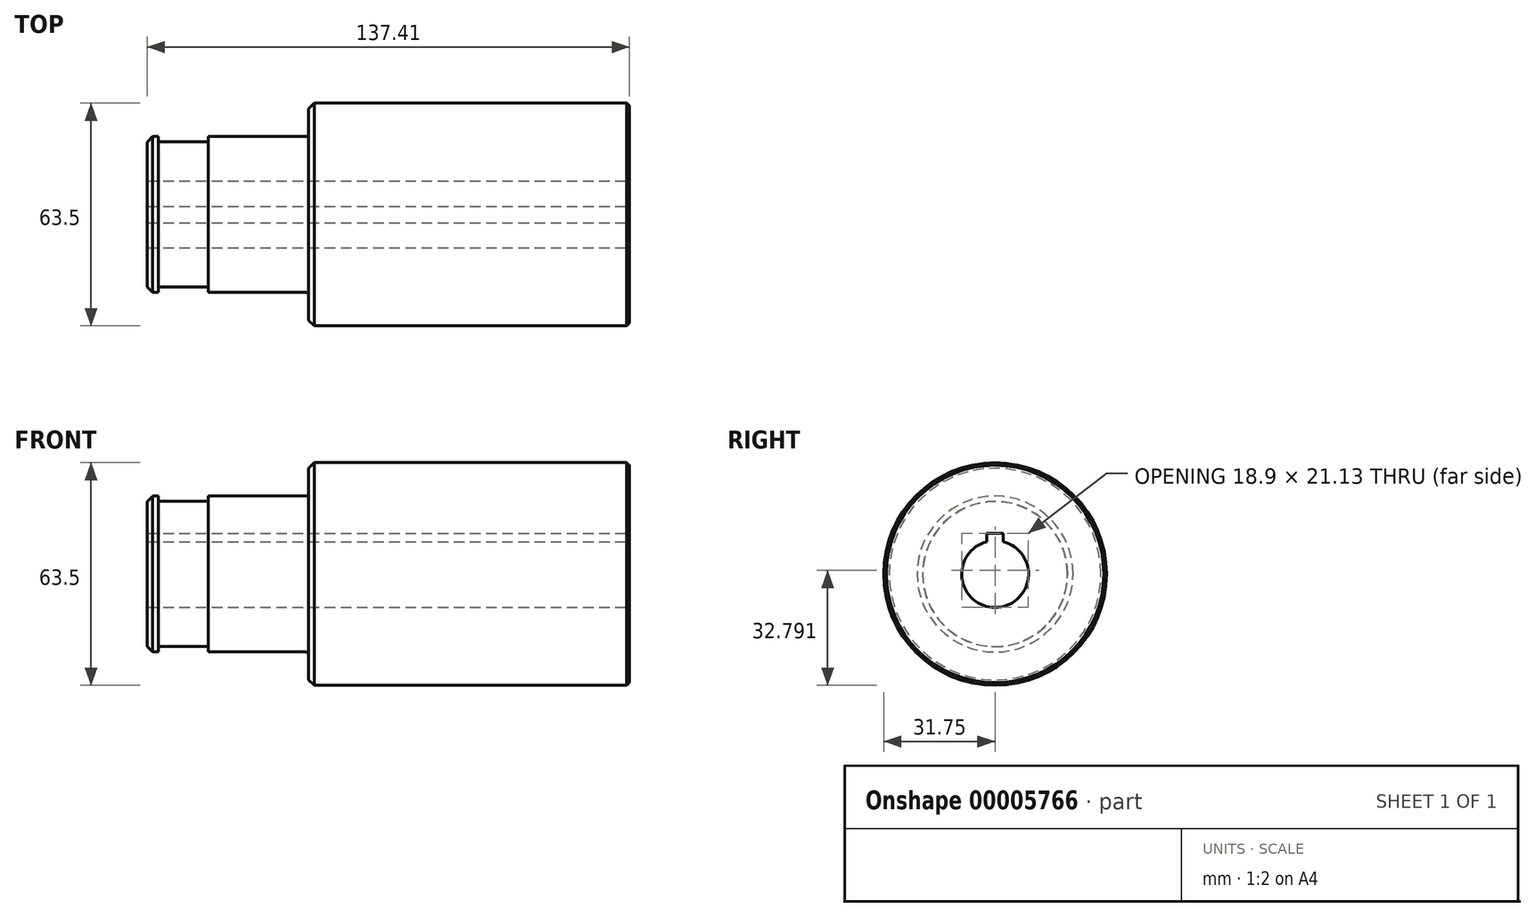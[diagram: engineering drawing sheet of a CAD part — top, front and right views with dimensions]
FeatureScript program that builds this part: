
annotation { "Feature Type Name" : "Feature", "Feature Type Description" : "" }
export const myFeature = defineFeature(function(context is Context, id is Id, definition is map)
    precondition{}
    {
        {
            var Q0;
            Q0=qCreatedBy(makeId("Front.planeOp"),FACE);
            var sketch = newSketch(context, id + "F0", { "sketchPlane" : qUnion([Q0])});
            skLineSegment(sketch, "E0", {"start": v(-137.41, 0) * mm, "end": v(0, 0) * mm});
            skLineSegment(sketch, "E1.0", {"start": v(-91.44, -31.75) * mm, "end": v(0, -31.75) * mm});
            skLineSegment(sketch, "E2", {"start": v(0, 0) * mm, "end": v(0, -31.75) * mm});
            skLineSegment(sketch, "E3.0", {"start": v(-91.44, -22.23) * mm, "end": v(-91.44, -31.75) * mm});
            skLineSegment(sketch, "E4.0", {"start": v(-137.41, -22.23) * mm, "end": v(-134.24, -22.23) * mm});
            skLineSegment(sketch, "E5.0", {"start": v(-137.41, 0) * mm, "end": v(-137.41, -22.23) * mm});
            skLineSegment(sketch, "E6.0", {"start": v(-134.24, -20.7) * mm, "end": v(-134.24, -22.23) * mm});
            skLineSegment(sketch, "E7.0", {"start": v(-120.02, -20.7) * mm, "end": v(-120.02, -22.23) * mm});
            skLineSegment(sketch, "E8.0", {"start": v(-134.24, -20.7) * mm, "end": v(-120.02, -20.7) * mm});
            skLineSegment(sketch, "E9.trimOffspring", {"start": v(-120.01, -22.23) * mm, "end": v(-91.44, -22.23) * mm});
            skPoint(sketch, "E10.orphan", {"position": v(-127.87, 0) * mm});
            skSolve(sketch);
        }
        {
            var Q0;
            Q0=makeQuery(id+"F0.imprint","IMPRINT",FACE,{"disambiguationData":[TD([[makeQuery(id+"F0.imprint","IMPRINT",EDGE,{"derivedFrom":sQuery(id+"F0.wireOp",EDGE,"E0")}),-1.0]])]});
            var Q1;
            Q1=sQuery(id+"F0.wireOp",EDGE,"E0");
            revolve(context, id + "F1", {"entities" : qUnion([Q0]), "axis" : qUnion([Q1]), "revolveType" : RevolveType.FULL});
        }
        {
            var Q0;
            Q0=makeQuery(id+"F1.opRevolve","SWEPT_EDGE",EDGE,{"disambiguationData":[OSD([sQuery(id+"F0.wireOp",EDGE,"E4.0"),sQuery(id+"F0.wireOp",EDGE,"E5.0")])]});
            chamfer(context, id + "F2", {"entities" : qUnion([Q0]), "width" : 1.59 * mm, "tangentPropagation" : true});
        }
        {
            var Q0;
            Q0=makeQuery(id+"F1.opRevolve","SWEPT_EDGE",EDGE,{"disambiguationData":[OSD([sQuery(id+"F0.wireOp",EDGE,"E1.0"),sQuery(id+"F0.wireOp",EDGE,"E3.0")])]});
            chamfer(context, id + "F3", {"entities" : qUnion([Q0]), "width" : 1.59 * mm, "tangentPropagation" : true});
        }
        {
            var Q0;
            Q0=makeQuery(id+"F1.opRevolve","SWEPT_EDGE",EDGE,{"disambiguationData":[OSD([sQuery(id+"F0.wireOp",EDGE,"E3.0"),sQuery(id+"F0.wireOp",EDGE,"E9.trimOffspring")])]});
            fillet(context, id + "F4", {"entities" : qUnion([Q0]), "radius" : 0.76 * mm, "tangentPropagation" : true, "allowEdgeOverflow" : false});
        }
        {
            var Q0;
            Q0=makeQuery(id+"F1.opRevolve","SWEPT_EDGE",EDGE,{"disambiguationData":[OSD([sQuery(id+"F0.wireOp",EDGE,"E1.0"),sQuery(id+"F0.wireOp",EDGE,"E2")])]});
            chamfer(context, id + "F5", {"entities" : qUnion([Q0]), "width" : 0.76 * mm, "tangentPropagation" : true});
        }
        {
            var Q0;
            Q0=makeQuery(id+"F1.opRevolve","SWEPT_FACE",FACE,{"disambiguationData":[OSD([sQuery(id+"F0.wireOp",EDGE,"E2")])]});
            var sketch = newSketch(context, id + "F6", { "sketchPlane" : qUnion([Q0])});
            skArc(sketch, "E11", {"start": v(-2.38, 9.22) * mm, "mid": v(0, -9.53) * mm, "end": v(2.38, 9.22) * mm});
            skLineSegment(sketch, "E12", {"start": v(0, 9.53) * mm, "end": v(0, -9.53) * mm, "construction": true});
            skLineSegment(sketch, "E13", {"start": v(0, -9.53) * mm, "end": v(-43.5, -9.53) * mm, "construction": true});
            skLineSegment(sketch, "E14", {"start": v(0, 9.53) * mm, "end": v(0, 35.97) * mm, "construction": true});
            skLineSegment(sketch, "E15.0", {"start": v(2.38, 11.6) * mm, "end": v(-2.38, 11.6) * mm});
            skLineSegment(sketch, "E16.0", {"start": v(-2.38, 9.22) * mm, "end": v(-2.38, 11.6) * mm});
            skLineSegment(sketch, "E17.0.MirrorCS", {"start": v(2.38, 9.22) * mm, "end": v(2.38, 11.6) * mm});
            skPoint(sketch, "E18.orphan", {"position": v(-2.38, 9.53) * mm});
            skPoint(sketch, "E19.orphan", {"position": v(2.38, 9.53) * mm});
            skPoint(sketch, "E20.orphan", {"position": v(-2.38, 35.97) * mm});
            skPoint(sketch, "E21.orphan", {"position": v(2.38, 35.97) * mm});
            skSolve(sketch);
        }
        {
            var Q0;
            Q0 = qSketchRegion(id + "F6", true);
            extrude(context, id + "F7", {"entities" : qUnion([Q0]), "operationType" : NewBodyOperationType.REMOVE, "endBound" : BoundingType.THROUGH_ALL, "oppositeDirection" : true, "depth" : 25.4 * mm});
        }
    });
